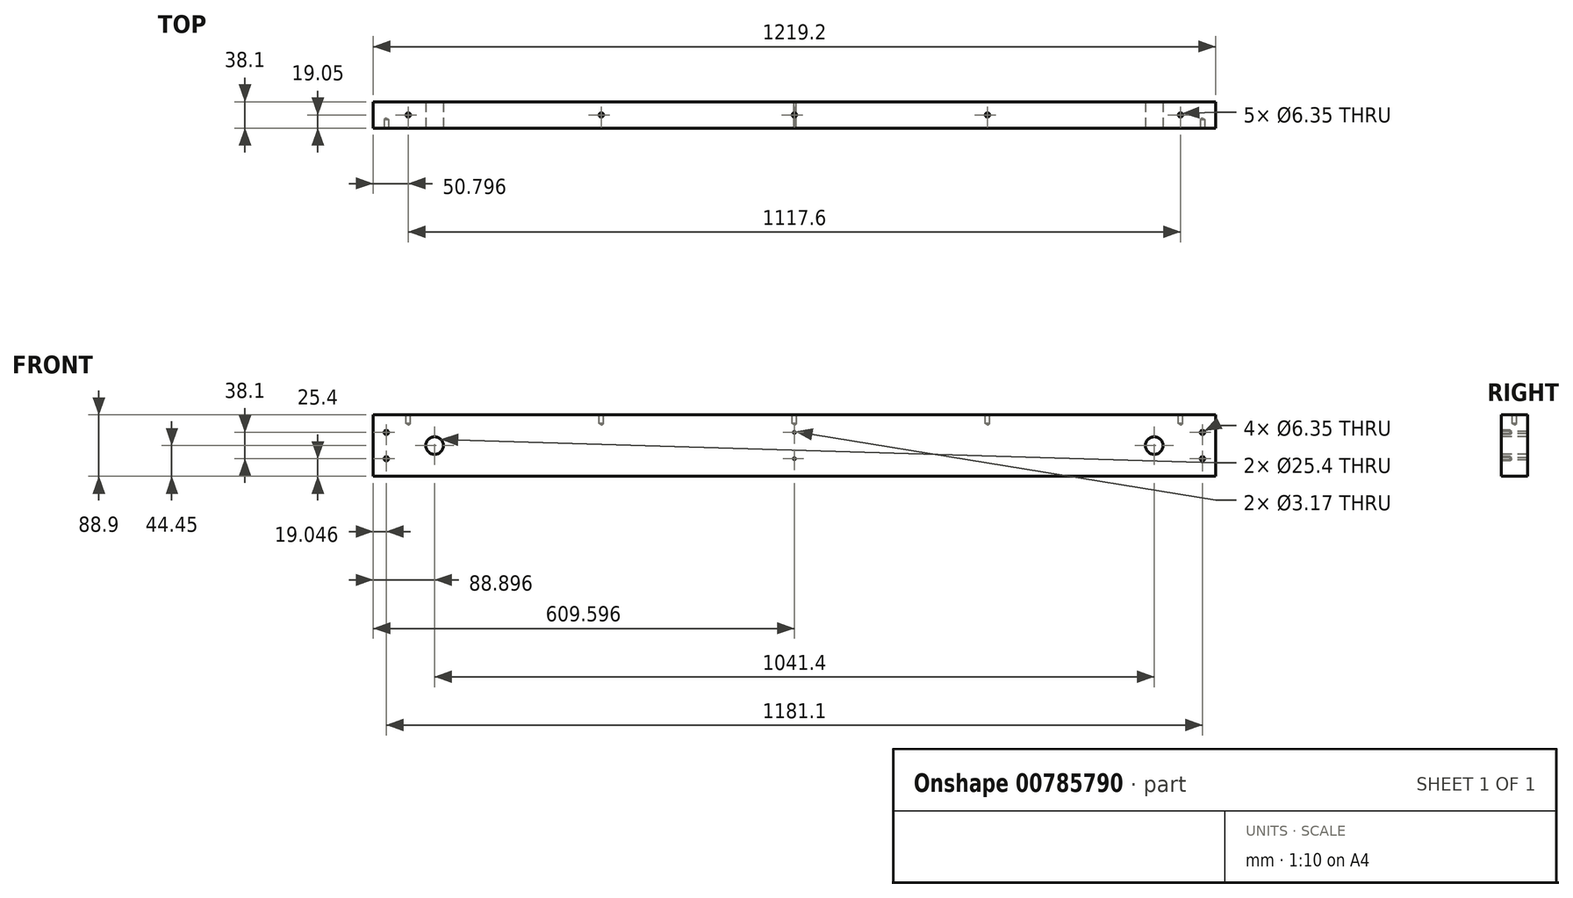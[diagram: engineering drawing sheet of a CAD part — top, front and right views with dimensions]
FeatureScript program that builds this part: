
annotation { "Feature Type Name" : "Feature", "Feature Type Description" : "" }
export const myFeature = defineFeature(function(context is Context, id is Id, definition is map)
    precondition{}
    {
        {
            var Q0;
            Q0=qCreatedBy(makeId("Front.planeOp"),FACE);
            var sketch = newSketch(context, id + "F0", { "sketchPlane" : qUnion([Q0])});
            skLineSegment(sketch, "E0.bottom", {"start": v(-634.12, 63.36) * mm, "end": v(585.08, 63.36) * mm});
            skLineSegment(sketch, "E0.top", {"start": v(-634.12, -25.54) * mm, "end": v(585.08, -25.54) * mm});
            skLineSegment(sketch, "E0.left", {"start": v(-634.12, 63.36) * mm, "end": v(-634.12, -25.54) * mm});
            skLineSegment(sketch, "E0.right", {"start": v(585.08, 63.36) * mm, "end": v(585.08, -25.54) * mm});
            skSolve(sketch);
        }
        {
            var Q0;
            Q0=makeQuery(id+"F0.imprint","IMPRINT",FACE,{"disambiguationData":[TD([[makeQuery(id+"F0.imprint","IMPRINT",EDGE,{"derivedFrom":sQuery(id+"F0.wireOp",EDGE,"E0.bottom")}),-1.0]])]});
            extrude(context, id + "F1", {"entities" : qUnion([Q0]), "depth" : 38.1 * mm, "offsetDistance" : 25.4 * mm});
        }
        {
            var Q0;
            Q0=makeQuery(id+"F1.opExtrude","CAP_FACE",FACE,{"disambiguationData":[OSD([sQuery(id+"F0.wireOp",EDGE,"E0.bottom"),sQuery(id+"F0.wireOp",EDGE,"E0.top"),sQuery(id+"F0.wireOp",EDGE,"E0.left"),sQuery(id+"F0.wireOp",EDGE,"E0.right")])],"isStart":false});
            var sketch = newSketch(context, id + "F2", { "sketchPlane" : qUnion([Q0])});
            skLineSegment(sketch, "E1", {"start": v(-24.52, -25.54) * mm, "end": v(-24.52, 63.36) * mm, "construction": true});
            skLineSegment(sketch, "E2", {"start": v(566.03, 63.36) * mm, "end": v(566.03, -25.54) * mm, "construction": true});
            skPoint(sketch, "E3", {"position": v(566.03, 37.96) * mm});
            skPoint(sketch, "E4", {"position": v(566.03, -0.14) * mm});
            skPoint(sketch, "E5.MirrorP", {"position": v(-615.07, 37.96) * mm});
            skPoint(sketch, "E6.MirrorP", {"position": v(-615.07, -0.14) * mm});
            skSolve(sketch);
        }
        {
            var Q0;
            Q0=sQuery(id+"F2.wireOp",VERTEX,"E3");
            var Q1;
            Q1=sQuery(id+"F2.wireOp",VERTEX,"E4");
            var Q2;
            Q2=sQuery(id+"F2.wireOp",VERTEX,"E5.MirrorP");
            var Q3;
            Q3=sQuery(id+"F2.wireOp",VERTEX,"E6.MirrorP");
            var Q4;
            Q4=makeQuery(id+"F1.opExtrude","SWEPT_BODY",BODY,{"disambiguationData":[OSD([sQuery(id+"F0.wireOp",EDGE,"E0.bottom"),sQuery(id+"F0.wireOp",EDGE,"E0.top"),sQuery(id+"F0.wireOp",EDGE,"E0.left"),sQuery(id+"F0.wireOp",EDGE,"E0.right")])]});
            hole(context, id + "F3", {"style" : HoleStyle.SIMPLE, "endStyle" : HoleEndStyle.BLIND, "holeDiameter" : 6.35 * mm, "majorDiameter" : 6.35 * mm, "holeDepth" : 12.7 * mm, "isTappedThrough" : true, "tappedDepth" : 12.7 * mm, "tapClearance" : 3, "locations" : qUnion([Q0, Q1, Q2, Q3]), "scope" : qUnion([Q4])});
        }
        {
            var Q0;
            Q0=makeQuery(id+"F1.opExtrude","SWEPT_FACE",FACE,{"disambiguationData":[OSD([sQuery(id+"F0.wireOp",EDGE,"E0.bottom")])]});
            var sketch = newSketch(context, id + "F4", { "sketchPlane" : qUnion([Q0])});
            skLineSegment(sketch, "E7", {"start": v(-634.12, -19.05) * mm, "end": v(585.08, -19.05) * mm, "construction": true});
            skPoint(sketch, "E8", {"position": v(-583.32, -19.05) * mm});
            skPoint(sketch, "E9", {"position": v(-303.92, -19.05) * mm});
            skPoint(sketch, "E10", {"position": v(-24.52, -19.05) * mm});
            skPoint(sketch, "E11", {"position": v(254.88, -19.05) * mm});
            skPoint(sketch, "E12", {"position": v(534.28, -19.05) * mm});
            skSolve(sketch);
        }
        {
            var Q0;
            Q0=sQuery(id+"F4.wireOp",VERTEX,"E8");
            var Q1;
            Q1=sQuery(id+"F4.wireOp",VERTEX,"E9");
            var Q2;
            Q2=sQuery(id+"F4.wireOp",VERTEX,"E10");
            var Q3;
            Q3=sQuery(id+"F4.wireOp",VERTEX,"E11");
            var Q4;
            Q4=sQuery(id+"F4.wireOp",VERTEX,"E12");
            var Q5;
            Q5=makeQuery(id+"F1.opExtrude","SWEPT_BODY",BODY,{"disambiguationData":[OSD([sQuery(id+"F0.wireOp",EDGE,"E0.bottom"),sQuery(id+"F0.wireOp",EDGE,"E0.top"),sQuery(id+"F0.wireOp",EDGE,"E0.left"),sQuery(id+"F0.wireOp",EDGE,"E0.right")])]});
            hole(context, id + "F5", {"style" : HoleStyle.SIMPLE, "endStyle" : HoleEndStyle.BLIND, "holeDiameter" : 6.35 * mm, "majorDiameter" : 6.35 * mm, "holeDepth" : 12.7 * mm, "isTappedThrough" : true, "tappedDepth" : 12.7 * mm, "tapClearance" : 3, "locations" : qUnion([Q0, Q1, Q2, Q3, Q4]), "scope" : qUnion([Q5])});
        }
        {
            var Q0;
            Q0=makeQuery(id+"F1.opExtrude","CAP_FACE",FACE,{"disambiguationData":[OSD([sQuery(id+"F0.wireOp",EDGE,"E0.bottom"),sQuery(id+"F0.wireOp",EDGE,"E0.top"),sQuery(id+"F0.wireOp",EDGE,"E0.left"),sQuery(id+"F0.wireOp",EDGE,"E0.right")])],"isStart":false});
            var sketch = newSketch(context, id + "F6", { "sketchPlane" : qUnion([Q0])});
            skLineSegment(sketch, "E13", {"start": v(-634.12, 18.91) * mm, "end": v(-370.31, 18.91) * mm, "construction": true});
            skPoint(sketch, "E13.startSnap0", {"position": v(-634.12, 18.91) * mm});
            skPoint(sketch, "E14", {"position": v(-545.22, 18.91) * mm});
            skLineSegment(sketch, "E15", {"start": v(-24.52, 63.36) * mm, "end": v(-24.52, -25.54) * mm, "construction": true});
            skPoint(sketch, "E16.MirrorP", {"position": v(496.18, 18.91) * mm});
            skSolve(sketch);
        }
        {
            var Q0;
            Q0=sQuery(id+"F6.wireOp",VERTEX,"E14");
            var Q1;
            Q1=sQuery(id+"F6.wireOp",VERTEX,"E16.MirrorP");
            var Q2;
            Q2=makeQuery(id+"F1.opExtrude","SWEPT_BODY",BODY,{"disambiguationData":[OSD([sQuery(id+"F0.wireOp",EDGE,"E0.bottom"),sQuery(id+"F0.wireOp",EDGE,"E0.top"),sQuery(id+"F0.wireOp",EDGE,"E0.left"),sQuery(id+"F0.wireOp",EDGE,"E0.right")])]});
            hole(context, id + "F7", {"style" : HoleStyle.SIMPLE, "endStyle" : HoleEndStyle.THROUGH, "holeDiameter" : 25.4 * mm, "majorDiameter" : 6.35 * mm, "isTappedThrough" : true, "tappedDepth" : 12.7 * mm, "tapClearance" : 3, "locations" : qUnion([Q0, Q1]), "scope" : qUnion([Q2])});
        }
        {
            var Q0;
            Q0=makeQuery(id+"F1.opExtrude","CAP_FACE",FACE,{"disambiguationData":[OSD([sQuery(id+"F0.wireOp",EDGE,"E0.bottom"),sQuery(id+"F0.wireOp",EDGE,"E0.top"),sQuery(id+"F0.wireOp",EDGE,"E0.left"),sQuery(id+"F0.wireOp",EDGE,"E0.right")])],"isStart":false});
            var sketch = newSketch(context, id + "F8", { "sketchPlane" : qUnion([Q0])});
            skLineSegment(sketch, "E17", {"start": v(-24.52, 63.36) * mm, "end": v(-24.52, -25.54) * mm, "construction": true});
            skPoint(sketch, "E18", {"position": v(-24.52, 37.96) * mm});
            skPoint(sketch, "E19", {"position": v(-24.52, -0.14) * mm});
            skSolve(sketch);
        }
        {
            var Q0;
            Q0=sQuery(id+"F8.wireOp",VERTEX,"E18");
            var Q1;
            Q1=sQuery(id+"F8.wireOp",VERTEX,"E19");
            var Q2;
            Q2=makeQuery(id+"F1.opExtrude","SWEPT_BODY",BODY,{"disambiguationData":[OSD([sQuery(id+"F0.wireOp",EDGE,"E0.bottom"),sQuery(id+"F0.wireOp",EDGE,"E0.top"),sQuery(id+"F0.wireOp",EDGE,"E0.left"),sQuery(id+"F0.wireOp",EDGE,"E0.right")])]});
            hole(context, id + "F9", {"style" : HoleStyle.SIMPLE, "endStyle" : HoleEndStyle.THROUGH, "holeDiameter" : 3.17 * mm, "majorDiameter" : 6.35 * mm, "isTappedThrough" : true, "tappedDepth" : 12.7 * mm, "tapClearance" : 3, "locations" : qUnion([Q0, Q1]), "scope" : qUnion([Q2])});
        }
    });
